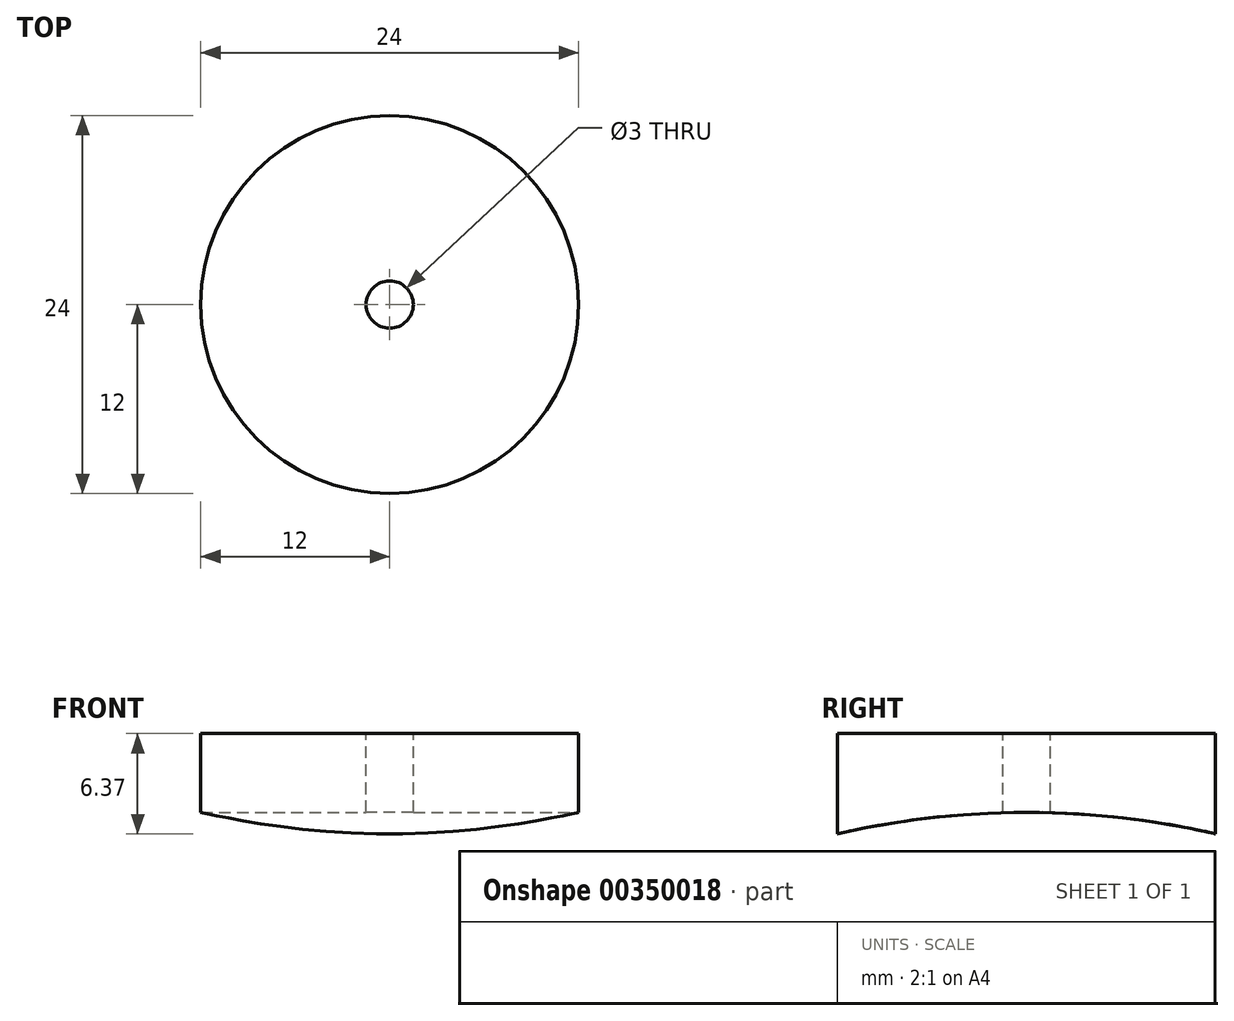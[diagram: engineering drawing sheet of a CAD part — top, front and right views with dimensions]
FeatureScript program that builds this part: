
annotation { "Feature Type Name" : "Feature", "Feature Type Description" : "" }
export const myFeature = defineFeature(function(context is Context, id is Id, definition is map)
    precondition{}
    {
        {
            var Q0;
            Q0=qCreatedBy(makeId("Top.planeOp"),FACE);
            var sketch = newSketch(context, id + "F0", { "sketchPlane" : qUnion([Q0])});
            skCircle(sketch, "E0", {"center": v(0, 0) * mm, "radius": 12 * mm});
            skLineSegment(sketch, "E1", {"start": v(0, 12) * mm, "end": v(0, -12) * mm, "construction": true});
            skSolve(sketch);
        }
        {
            var Q0;
            Q0=makeQuery(id+"F0.imprint","IMPRINT",FACE,{"disambiguationData":[TD([[makeQuery(id+"F0.imprint","IMPRINT",EDGE,{"derivedFrom":sQuery(id+"F0.wireOp",EDGE,"E0")}),1.0]])]});
            extrude(context, id + "F1", {"entities" : qUnion([Q0]), "endBound" : BoundingType.SYMMETRIC, "depth" : 10 * mm});
        }
        {
            var Q0;
            Q0=qCreatedBy(makeId("Right.planeOp"),FACE);
            var sketch = newSketch(context, id + "F2", { "sketchPlane" : qUnion([Q0])});
            skLineSegment(sketch, "E2", {"start": v(0, 0) * mm, "end": v(0, -88.13) * mm, "construction": true});
            skCircle(sketch, "E3", {"center": v(0, -53.4) * mm, "radius": 53.4 * mm});
            skSolve(sketch);
        }
        {
            var Q0;
            Q0=makeQuery(id+"F2.imprint","IMPRINT",FACE,{"disambiguationData":[TD([[makeQuery(id+"F2.imprint","IMPRINT",EDGE,{"derivedFrom":sQuery(id+"F2.wireOp",EDGE,"E3")}),1.0]])]});
            extrude(context, id + "F3", {"entities" : qUnion([Q0]), "operationType" : NewBodyOperationType.REMOVE, "endBound" : BoundingType.SYMMETRIC, "oppositeDirection" : true, "depth" : 25 * mm});
        }
        {
            var Q0;
            Q0=makeQuery(id+"F1.opExtrude","CAP_FACE",FACE,{"disambiguationData":[OSD([sQuery(id+"F0.wireOp",EDGE,"E0")])],"isStart":false});
            var sketch = newSketch(context, id + "F4", { "sketchPlane" : qUnion([Q0])});
            skCircle(sketch, "E4", {"center": v(0, 0) * mm, "radius": 1.5 * mm});
            skSolve(sketch);
        }
        {
            var Q0;
            Q0=makeQuery(id+"F4.imprint","IMPRINT",FACE,{"disambiguationData":[TD([[makeQuery(id+"F4.imprint","IMPRINT",EDGE,{"derivedFrom":sQuery(id+"F4.wireOp",EDGE,"E4")}),1.0]])]});
            extrude(context, id + "F5", {"entities" : qUnion([Q0]), "operationType" : NewBodyOperationType.REMOVE, "endBound" : BoundingType.THROUGH_ALL, "oppositeDirection" : true, "depth" : 25 * mm});
        }
    });
